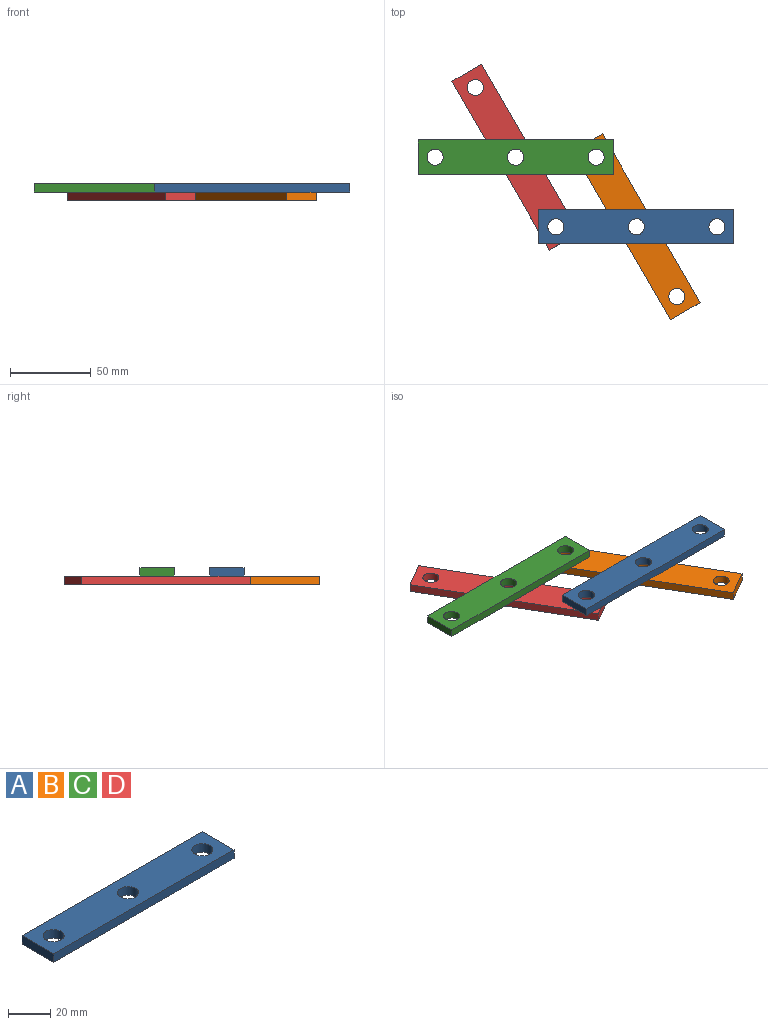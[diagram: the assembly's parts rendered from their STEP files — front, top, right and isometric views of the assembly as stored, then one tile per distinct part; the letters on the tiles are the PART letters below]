
ASSEMBLY  parts=4 mates=4
PART A: 9 faces, bbox 121.1x21.3x5 mm
  f0: plane 121.11x5mm, normal (0,1,0), area 605.5mm2, adj f1,f6,f7,f8
  f1: plane 21.32x5mm, normal (-1,0,0), area 106.6mm2, adj f0,f2,f7,f8
  f2: plane 121.11x5mm, normal (0,-1,0), area 605.5mm2, adj f1,f6,f7,f8
  f3: cylinder r=5mm len=10mm, axis (0,0,-1), area 157.1mm2, adj f7,f8
  f4: cylinder r=5mm len=10mm, axis (0,0,-1), area 157.1mm2, adj f7,f8
  f5: cylinder r=5mm len=10mm, axis (0,0,-1), area 157.1mm2, adj f7,f8
  f6: plane 21.32x5mm, normal (1,0,0), area 106.6mm2, adj f0,f2,f7,f8
  f7: plane 121.11x21.32mm, normal (0,0,1), area 2346mm2, adj f0,f1,f2,f3,f4,f5,f6
  f8: plane 121.11x21.32mm, normal (0,0,-1), area 2346mm2, adj f0,f1,f2,f3,f4,f5,f6
PART B: same geometry as A
PART C: same geometry as A
PART D: same geometry as A
PLACE A t=(-2.32,111.64,-67.45)mm fixed
PLACE B rot(axis=(0,0,1),120.1deg) t=(-2.32,111.64,-72.45)mm
PLACE C t=(-77.37,154.91,-67.45)mm
PLACE D rot(axis=(0,0,1),120.1deg) t=(-77.37,154.91,-72.45)mm
MATE revolute C.f5 <-> B.f5  axis (0,0,-1) through (-27.37,154.91,-69.95)mm
MATE revolute A.f3 <-> B.f3  axis (0,0,-1) through (-2.32,111.64,-69.95)mm
MATE revolute A.f4 <-> D.f4  axis (0,0,-1) through (-52.32,111.64,-69.95)mm
MATE revolute C.f3 <-> D.f3  axis (0,0,-1) through (-77.37,154.91,-69.95)mm
